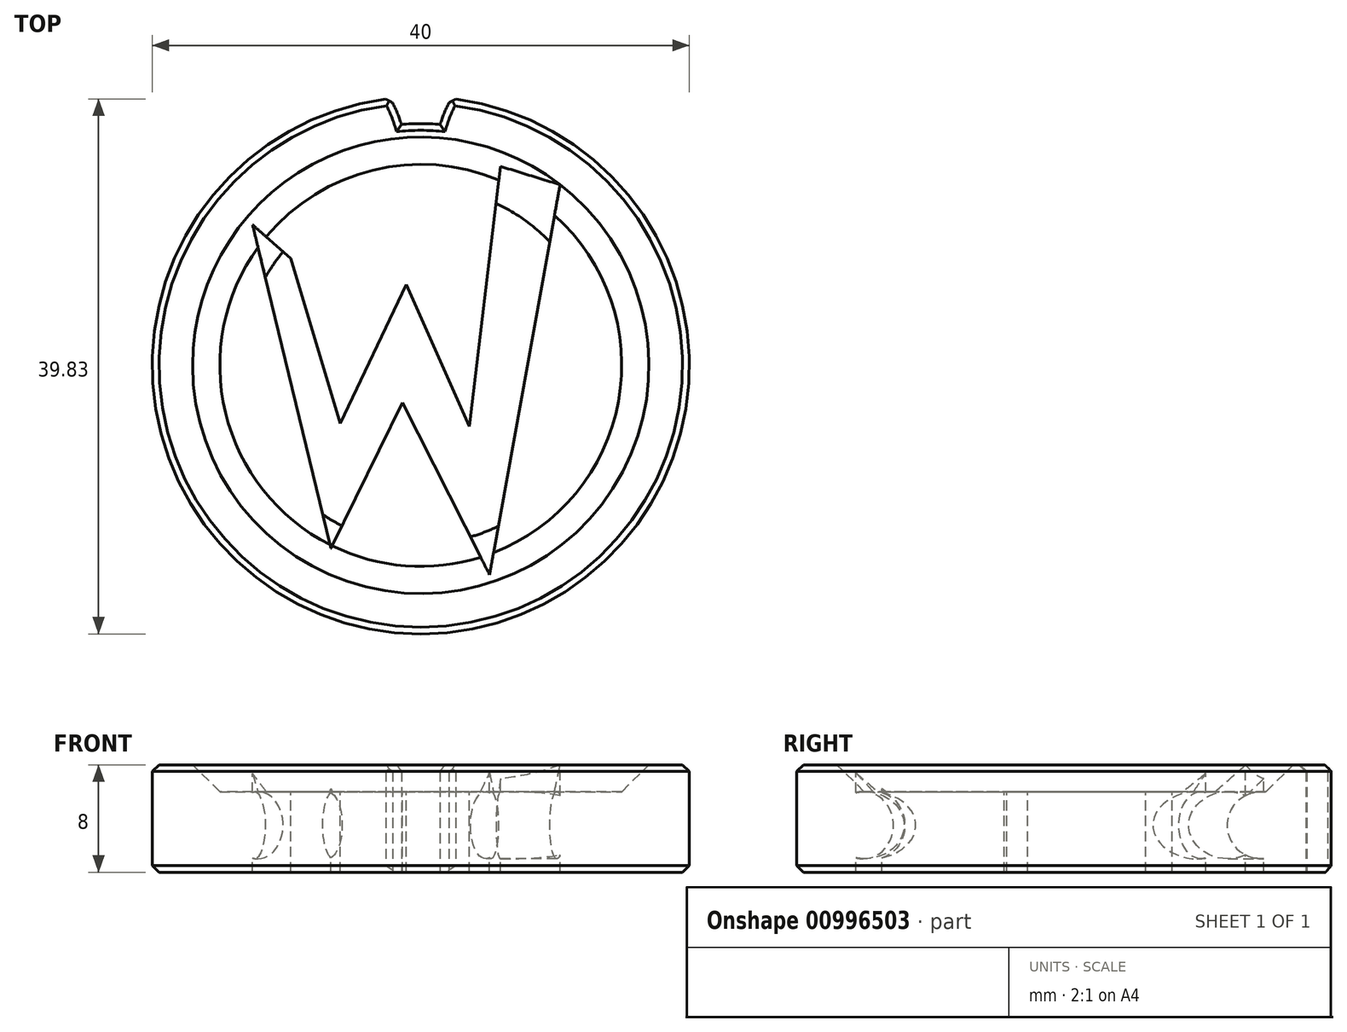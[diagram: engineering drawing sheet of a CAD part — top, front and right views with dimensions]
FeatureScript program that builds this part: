
annotation { "Feature Type Name" : "Feature", "Feature Type Description" : "" }
export const myFeature = defineFeature(function(context is Context, id is Id, definition is map)
    precondition{}
    {
        {
            var Q0;
            Q0=qCreatedBy(makeId("Front.planeOp"),FACE);
            var sketch = newSketch(context, id + "F0", { "sketchPlane" : qUnion([Q0])});
            skLineSegment(sketch, "E0", {"start": v(0, 0) * mm, "end": v(-17, 0) * mm});
            skLineSegment(sketch, "E1", {"start": v(0, 0) * mm, "end": v(0, 6) * mm});
            skLineSegment(sketch, "E2", {"start": v(-17, 0) * mm, "end": v(-20, 0) * mm});
            skLineSegment(sketch, "E3", {"start": v(-20, 0) * mm, "end": v(-20, 8) * mm});
            skLineSegment(sketch, "E4", {"start": v(-20, 8) * mm, "end": v(-17, 8) * mm});
            skLineSegment(sketch, "E5", {"start": v(-17, 8) * mm, "end": v(-14.97, 6) * mm});
            skLineSegment(sketch, "E6", {"start": v(-14.97, 6) * mm, "end": v(0, 6) * mm});
            skSolve(sketch);
        }
        {
            var Q0;
            Q0=makeQuery(id+"F0.imprint","IMPRINT",FACE,{"disambiguationData":[TD([[makeQuery(id+"F0.imprint","IMPRINT",EDGE,{"derivedFrom":sQuery(id+"F0.wireOp",EDGE,"E0")}),-1.0]])]});
            var Q1;
            Q1=sQuery(id+"F0.wireOp",EDGE,"E1");
            revolve(context, id + "F1", {"surfaceOperationType" : NewSurfaceOperationType.NEW, "entities" : qUnion([Q0]), "axis" : qUnion([Q1]), "revolveType" : RevolveType.FULL});
        }
        {
            var Q0;
            Q0=makeQuery(id+"F1.opRevolve","SWEPT_EDGE",EDGE,{"disambiguationData":[OSD([sQuery(id+"F0.wireOp",EDGE,"E3"),sQuery(id+"F0.wireOp",EDGE,"E4")])]});
            var Q1;
            Q1=makeQuery(id+"F1.opRevolve","SWEPT_EDGE",EDGE,{"disambiguationData":[OSD([sQuery(id+"F0.wireOp",EDGE,"E2"),sQuery(id+"F0.wireOp",EDGE,"E3")])]});
            chamfer(context, id + "F2", {"entities" : qUnion([Q0, Q1]), "width" : 0.5 * mm, "tangentPropagation" : true});
        }
        {
            var Q0;
            Q0=qCreatedBy(makeId("Top.planeOp"),FACE);
            cPlane(context, id + "F3", {"entities" : qUnion([Q0]), "cplaneType" : CPlaneType.OFFSET, "offset" : 10 * mm, "width" : 150 * mm, "height" : 150 * mm});
        }
        {
            var Q0;
            Q0=qCreatedBy(id+"F3.planeOp",FACE);
            var sketch = newSketch(context, id + "F4", { "sketchPlane" : qUnion([Q0])});
            skLineSegment(sketch, "E7", {"start": v(-12.53, 10.47) * mm, "end": v(-6.7, -13.65) * mm});
            skLineSegment(sketch, "E8", {"start": v(-6.7, -13.65) * mm, "end": v(-1.35, -2.77) * mm});
            skLineSegment(sketch, "E9", {"start": v(-1.35, -2.77) * mm, "end": v(5.12, -15.6) * mm});
            skLineSegment(sketch, "E10", {"start": v(5.12, -15.6) * mm, "end": v(10.37, 13.45) * mm});
            skLineSegment(sketch, "E11", {"start": v(10.37, 13.45) * mm, "end": v(5.94, 14.82) * mm});
            skLineSegment(sketch, "E12", {"start": v(5.94, 14.82) * mm, "end": v(3.62, -4.55) * mm});
            skLineSegment(sketch, "E13", {"start": v(3.62, -4.55) * mm, "end": v(-1.08, 6.02) * mm});
            skLineSegment(sketch, "E14", {"start": v(-1.08, 6.02) * mm, "end": v(-6, -4.34) * mm});
            skLineSegment(sketch, "E15", {"start": v(-6, -4.34) * mm, "end": v(-9.69, 7.96) * mm});
            skLineSegment(sketch, "E16", {"start": v(-9.69, 7.96) * mm, "end": v(-12.53, 10.47) * mm});
            skSolve(sketch);
        }
        {
            var Q0;
            Q0 = qSketchRegion(id + "F4", true);
            extrude(context, id + "F5", {"entities" : qUnion([Q0]), "operationType" : NewBodyOperationType.REMOVE, "oppositeDirection" : true, "depth" : 25 * mm, "offsetDistance" : 25 * mm});
        }
        {
            var Q0;
            Q0=qCreatedBy(makeId("Front.planeOp"),FACE);
            var sketch = newSketch(context, id + "F6", { "sketchPlane" : qUnion([Q0])});
            skCircle(sketch, "E17", {"center": v(-15.8, 3.5) * mm, "radius": 2.5 * mm});
            skSolve(sketch);
        }
        {
            var Q0;
            Q0 = qSketchRegion(id + "F6", true);
            var Q1;
            Q1=sQuery(id+"F0.wireOp",EDGE,"E1");
            revolve(context, id + "F7", {"operationType" : NewBodyOperationType.ADD, "surfaceOperationType" : NewSurfaceOperationType.NEW, "entities" : qUnion([Q0]), "axis" : qUnion([Q1]), "revolveType" : RevolveType.FULL});
        }
        {
            var Q0;
            Q0=qCreatedBy(makeId("Top.planeOp"),FACE);
            var sketch = newSketch(context, id + "F8", { "sketchPlane" : qUnion([Q0])});
            skArc(sketch, "E18", {"start": v(-1.44, 17.94) * mm, "mid": v(-2.79, 20.7) * mm, "end": v(-4.9, 22.93) * mm});
            skArc(sketch, "E19.MirrorC", {"start": v(1.44, 17.94) * mm, "mid": v(2.79, 20.7) * mm, "end": v(4.9, 22.93) * mm});
            skArc(sketch, "E20", {"start": v(1.44, 17.94) * mm, "mid": v(0, 18) * mm, "end": v(-1.44, 17.94) * mm});
            skLineSegment(sketch, "E21", {"start": v(-4.9, 22.93) * mm, "end": v(4.9, 22.93) * mm});
            skSolve(sketch);
        }
        {
            var Q0;
            Q0 = qSketchRegion(id + "F8", true);
            extrude(context, id + "F9", {"entities" : qUnion([Q0]), "operationType" : NewBodyOperationType.REMOVE, "endBound" : BoundingType.THROUGH_ALL, "depth" : 25 * mm, "offsetDistance" : 25 * mm});
        }
        {
            var Q0;
            Q0=makeQuery(id+"F9.boolean.opBoolean","INTERSECT",EDGE,{"derivedFrom":[makeQuery(id+"F1.opRevolve","SWEPT_FACE",FACE,{"disambiguationData":[OSD([sQuery(id+"F0.wireOp",EDGE,"E4")])]}),makeQuery(id+"F9.opExtrude","SWEPT_FACE",FACE,{"disambiguationData":[OSD([sQuery(id+"F8.wireOp",EDGE,"E18")])]})]});
            var Q1;
            Q1=makeQuery(id+"F9.boolean.opBoolean","INTERSECT",EDGE,{"derivedFrom":[makeQuery(id+"F1.opRevolve","SWEPT_FACE",FACE,{"disambiguationData":[OSD([sQuery(id+"F0.wireOp",EDGE,"E3")])]}),makeQuery(id+"F9.opExtrude","SWEPT_FACE",FACE,{"disambiguationData":[OSD([sQuery(id+"F8.wireOp",EDGE,"E18")])]})]});
            var Q2;
            Q2=makeQuery(id+"F9.boolean.opBoolean","COPY",EDGE,{"derivedFrom":makeQuery(id+"F9.opExtrude","CAP_EDGE",EDGE,{"disambiguationData":[OSD([sQuery(id+"F8.wireOp",EDGE,"E18")])],"isStart":true})});
            var Q3;
            Q3=makeQuery(id+"F9.boolean.opBoolean","COPY",EDGE,{"derivedFrom":makeQuery(id+"F9.opExtrude","CAP_EDGE",EDGE,{"disambiguationData":[OSD([sQuery(id+"F8.wireOp",EDGE,"E20")])],"isStart":true})});
            var Q4;
            Q4=makeQuery(id+"F9.boolean.opBoolean","INTERSECT",EDGE,{"derivedFrom":[makeQuery(id+"F1.opRevolve","SWEPT_FACE",FACE,{"disambiguationData":[OSD([sQuery(id+"F0.wireOp",EDGE,"E4")])]}),makeQuery(id+"F9.opExtrude","SWEPT_FACE",FACE,{"disambiguationData":[OSD([sQuery(id+"F8.wireOp",EDGE,"E20")])]})]});
            var Q5;
            Q5=makeQuery(id+"F9.boolean.opBoolean","COPY",EDGE,{"derivedFrom":makeQuery(id+"F9.opExtrude","CAP_EDGE",EDGE,{"disambiguationData":[OSD([sQuery(id+"F8.wireOp",EDGE,"E19.MirrorC")])],"isStart":true})});
            var Q6;
            Q6=makeQuery(id+"F9.boolean.opBoolean","INTERSECT",EDGE,{"derivedFrom":[makeQuery(id+"F1.opRevolve","SWEPT_FACE",FACE,{"disambiguationData":[OSD([sQuery(id+"F0.wireOp",EDGE,"E3")])]}),makeQuery(id+"F9.opExtrude","SWEPT_FACE",FACE,{"disambiguationData":[OSD([sQuery(id+"F8.wireOp",EDGE,"E19.MirrorC")])]})]});
            var Q7;
            Q7=makeQuery(id+"F9.boolean.opBoolean","INTERSECT",EDGE,{"derivedFrom":[makeQuery(id+"F1.opRevolve","SWEPT_FACE",FACE,{"disambiguationData":[OSD([sQuery(id+"F0.wireOp",EDGE,"E4")])]}),makeQuery(id+"F9.opExtrude","SWEPT_FACE",FACE,{"disambiguationData":[OSD([sQuery(id+"F8.wireOp",EDGE,"E19.MirrorC")])]})]});
            chamfer(context, id + "F10", {"entities" : qUnion([Q0, Q1, Q2, Q3, Q4, Q5, Q6, Q7]), "width" : 0.5 * mm, "tangentPropagation" : true});
        }
    });
